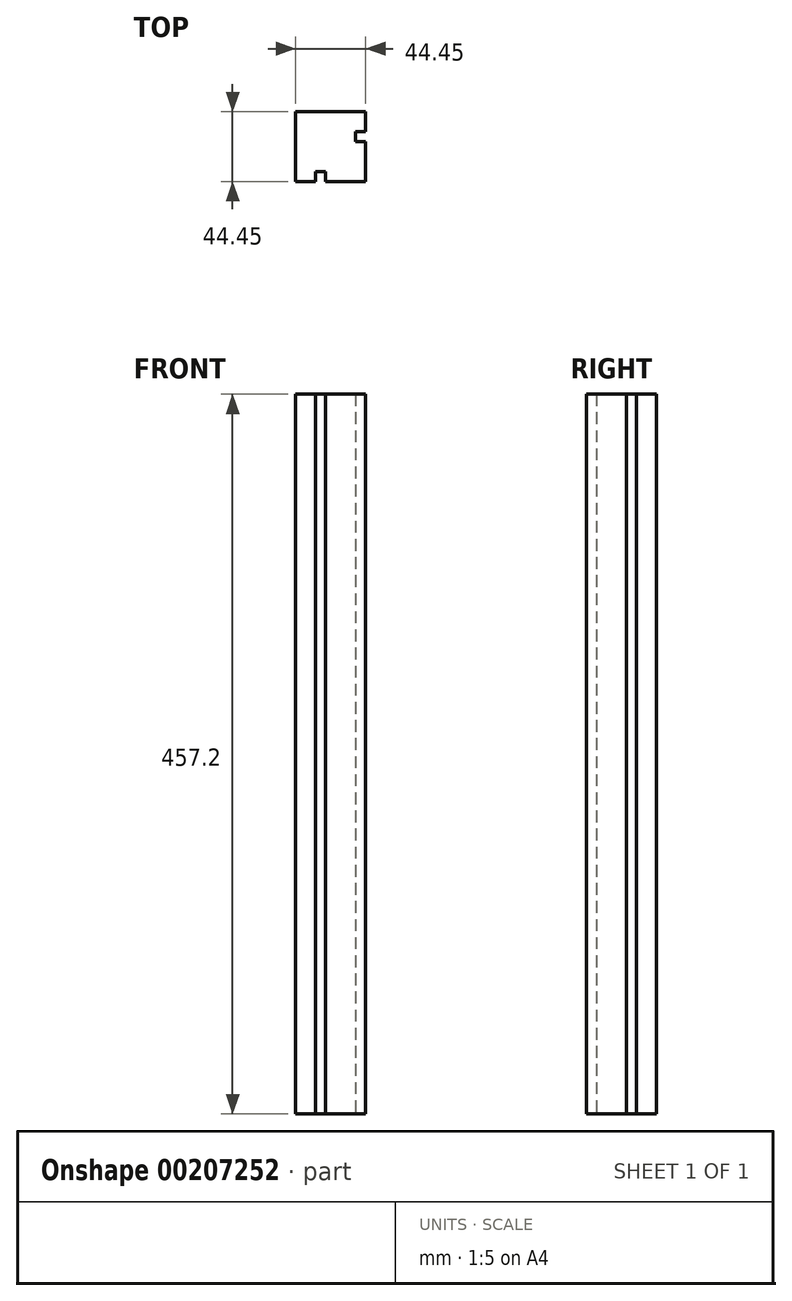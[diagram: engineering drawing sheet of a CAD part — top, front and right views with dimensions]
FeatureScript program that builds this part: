
annotation { "Feature Type Name" : "Feature", "Feature Type Description" : "" }
export const myFeature = defineFeature(function(context is Context, id is Id, definition is map)
    precondition{}
    {
        {
            var Q0;
            Q0=qCreatedBy(makeId("Top.planeOp"),FACE);
            var sketch = newSketch(context, id + "F0", { "sketchPlane" : qUnion([Q0])});
            skLineSegment(sketch, "E0", {"start": v(0, 0) * mm, "end": v(0, 44.45) * mm});
            skLineSegment(sketch, "E1", {"start": v(0, 44.45) * mm, "end": v(44.45, 44.45) * mm});
            skLineSegment(sketch, "E2", {"start": v(44.45, 44.45) * mm, "end": v(44.45, 31.75) * mm});
            skLineSegment(sketch, "E3", {"start": v(44.45, 31.75) * mm, "end": v(38.1, 31.75) * mm});
            skLineSegment(sketch, "E4", {"start": v(38.1, 31.75) * mm, "end": v(38.1, 25.4) * mm});
            skLineSegment(sketch, "E5", {"start": v(38.1, 25.4) * mm, "end": v(44.45, 25.4) * mm});
            skLineSegment(sketch, "E6", {"start": v(44.45, 25.4) * mm, "end": v(44.45, 0) * mm});
            skLineSegment(sketch, "E7", {"start": v(44.45, 0) * mm, "end": v(19.05, 0) * mm});
            skLineSegment(sketch, "E8", {"start": v(19.05, 0) * mm, "end": v(19.05, 6.35) * mm});
            skLineSegment(sketch, "E9", {"start": v(19.05, 6.35) * mm, "end": v(12.7, 6.35) * mm});
            skLineSegment(sketch, "E10", {"start": v(12.7, 6.35) * mm, "end": v(12.7, 0) * mm});
            skLineSegment(sketch, "E11", {"start": v(12.7, 0) * mm, "end": v(0, 0) * mm});
            skSolve(sketch);
        }
        {
            var Q0;
            Q0 = qSketchRegion(id + "F0", true);
            extrude(context, id + "F1", {"entities" : qUnion([Q0]), "depth" : 457.2 * mm});
        }
    });
